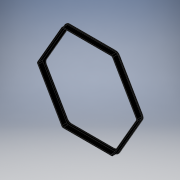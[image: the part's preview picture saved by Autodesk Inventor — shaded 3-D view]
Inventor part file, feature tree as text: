
AUTODESK INVENTOR PART (.ipt)
format: ipt  version: 2019 (Build 230136000, 136)  size: 187,392 bytes
history: native  units: mm
features: extrude x3, sketch x3, fillet x2, projected_geometry x2
ambient origin geometry x8: Origin, YZ Plane, XZ Plane, XY Plane, X Axis, Y Axis, Z Axis, Center Point
bodies: Solid1 (feature_tree)
feature tree (10):
  extrude  "Extrusion1"  Depth=2.0mm TaperAngle=0.0deg
  extrude  "Extrusion5"  Depth=2.0mm
  extrude  "Extrusion6"  Depth=4.0mm
  fillet  "Fillet1"  Radius=7.0mm
  fillet  "Fillet2"  Radius=10.0mm
  sketch  "Sketch1"  dims[d0=200.0mm d1=2.0mm d2=0.0mm]
  sketch  "Sketch5"  dims[d15=2.0mm d16=2.0mm]
  projected_geometry  "Projected Loop4"
  sketch  "Sketch7"  dims[d17=10.0mm d18=0.0mm d19=4.0mm d20=7.0mm d21=0.0mm d22=10.0mm d23=4.0mm d24=10.0mm]
  projected_geometry  "Projected Loop6"
